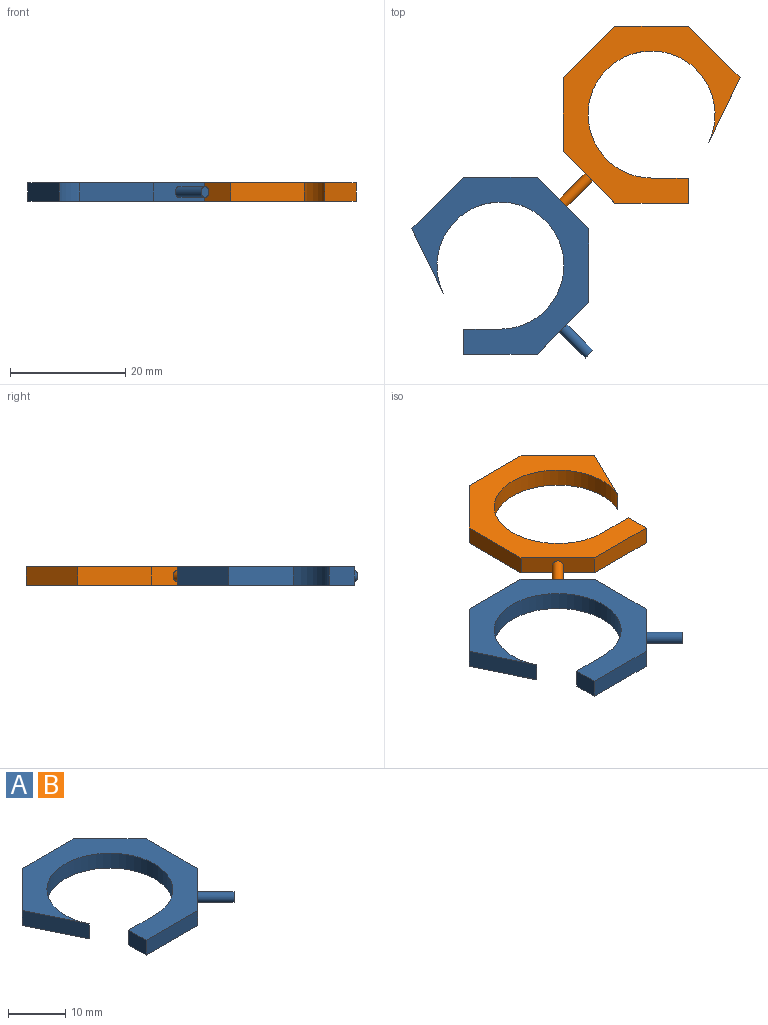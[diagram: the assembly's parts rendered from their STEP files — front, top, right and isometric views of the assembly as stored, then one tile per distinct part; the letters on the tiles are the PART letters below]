
ASSEMBLY  parts=2 mates=1
PART A: 14 faces, bbox 31.3x31.3x3.2 mm
  f0: plane 8.98x8.98mm, normal (-0.71,0.71,0), area 40.3mm2, adj f1,f9,f10,f11
  f1: plane 11.17x5.44mm, normal (-0.9,-0.44,0), area 39.4mm2, adj f0,f2,f10,f11
  f2: cylinder r=11mm len=22mm, axis (0,0,-1), area 180.4mm2, adj f1,f3,f10,f11
  f3: plane 6.35x3.18mm, normal (0,1,0), area 20.2mm2, adj f2,f4,f10,f11
  f4: plane 4.33x3.18mm, normal (-1,0,0), area 13.7mm2, adj f3,f5,f10,f11
  f5: plane 12.7x3.18mm, normal (0,-1,0), area 40.3mm2, adj f4,f6,f10,f11
  f6: plane 8.98x8.98mm, normal (0.71,-0.71,0), area 37.5mm2, adj f5,f7,f10,f11,f12
  f7: plane 12.7x3.18mm, normal (1,0,0), area 40.3mm2, adj f6,f8,f10,f11
  f8: plane 8.98x8.98mm, normal (0.71,0.71,0), area 40.3mm2, adj f7,f9,f10,f11
  f9: plane 12.7x3.18mm, normal (0,1,0), area 40.3mm2, adj f0,f8,f10,f11
  f10: plane 30.66x30.66mm, normal (0,0,1), area 318.7mm2, adj f0,f1,f2,f3,f4,f5,f6,f7
  f11: plane 30.66x30.66mm, normal (0,0,-1), area 318.7mm2, adj f0,f1,f2,f3,f4,f5,f6,f7
  f12: cylinder r=0.95mm len=5.84mm, axis (-0.71,0.71,0), area 38mm2, adj f6,f13
  f13: plane 1.91x1.35mm, normal (0.71,-0.71,0), area 2.9mm2, adj f12
PART B: same geometry as A
PLACE A t=(-6.31,-15.24,-1.49)mm
PLACE B rot(axis=(0,1,0),180deg) t=(32.56,10.93,1.69)mm
MATE fastened B.f12 <-> A.f8  axis (-0.71,-0.71,0) through (10.88,10.93,0.1)mm
